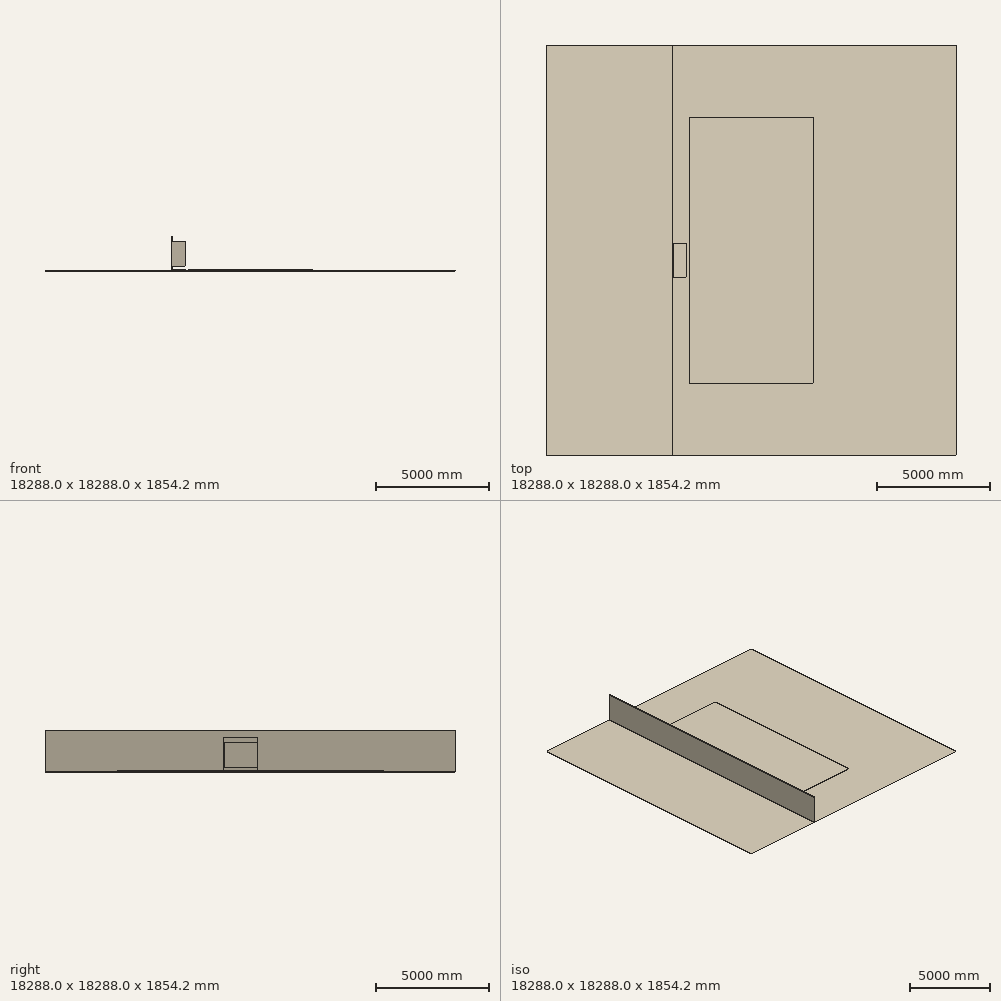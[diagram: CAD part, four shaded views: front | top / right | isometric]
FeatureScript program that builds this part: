
annotation { "Feature Type Name" : "Feature", "Feature Type Description" : "" }
export const myFeature = defineFeature(function(context is Context, id is Id, definition is map)
    precondition{}
    {
        {
            var Q0;
            Q0=qCreatedBy(makeId("Top.planeOp"),FACE);
            var sketch = newSketch(context, id + "F0", { "sketchPlane" : qUnion([Q0])});
            skLineSegment(sketch, "E0.bottom", {"start": v(-9144, 9144) * mm, "end": v(9144, 9144) * mm});
            skLineSegment(sketch, "E0.top", {"start": v(-9144, -9144) * mm, "end": v(9144, -9144) * mm});
            skLineSegment(sketch, "E0.left", {"start": v(-9144, 9144) * mm, "end": v(-9144, -9144) * mm});
            skLineSegment(sketch, "E0.right", {"start": v(9144, 9144) * mm, "end": v(9144, -9144) * mm});
            skSolve(sketch);
        }
        {
            var Q0;
            Q0=makeQuery(id+"F0.imprint","IMPRINT",FACE,{"disambiguationData":[TD([[makeQuery(id+"F0.imprint","IMPRINT",EDGE,{"derivedFrom":sQuery(id+"F0.wireOp",EDGE,"E0.bottom")}),-1.0]])]});
            extrude(context, id + "F1", {"entities" : qUnion([Q0]), "depth" : 25.4 * mm});
        }
        {
            var Q0;
            Q0=makeQuery(id+"F1.opExtrude","CAP_FACE",FACE,{"disambiguationData":[OSD([sQuery(id+"F0.wireOp",EDGE,"E0.bottom"),sQuery(id+"F0.wireOp",EDGE,"E0.top"),sQuery(id+"F0.wireOp",EDGE,"E0.left"),sQuery(id+"F0.wireOp",EDGE,"E0.right")])],"isStart":false});
            var sketch = newSketch(context, id + "F2", { "sketchPlane" : qUnion([Q0])});
            skLineSegment(sketch, "E1.bottom", {"start": v(-2743.2, 5943.6) * mm, "end": v(2743.2, 5943.6) * mm});
            skLineSegment(sketch, "E1.top", {"start": v(-2743.2, -5943.6) * mm, "end": v(2743.2, -5943.6) * mm});
            skLineSegment(sketch, "E1.left", {"start": v(-2743.2, 5943.6) * mm, "end": v(-2743.2, -5943.6) * mm});
            skLineSegment(sketch, "E1.right", {"start": v(2743.2, 5943.6) * mm, "end": v(2743.2, -5943.6) * mm});
            skSolve(sketch);
        }
        {
            var Q0;
            Q0=makeQuery(id+"F2.imprint","IMPRINT",FACE,{"disambiguationData":[TD([[makeQuery(id+"F2.imprint","IMPRINT",EDGE,{"derivedFrom":sQuery(id+"F2.wireOp",EDGE,"E1.bottom")}),-1.0]])]});
            extrude(context, id + "F3", {"entities" : qUnion([Q0]), "operationType" : NewBodyOperationType.ADD, "depth" : 50.8 * mm});
        }
        {
            var Q0;
            Q0=makeQuery(id+"F1.opExtrude","CAP_FACE",FACE,{"disambiguationData":[OSD([sQuery(id+"F0.wireOp",EDGE,"E0.bottom"),sQuery(id+"F0.wireOp",EDGE,"E0.top"),sQuery(id+"F0.wireOp",EDGE,"E0.left"),sQuery(id+"F0.wireOp",EDGE,"E0.right")])],"isStart":false});
            var sketch = newSketch(context, id + "F4", { "sketchPlane" : qUnion([Q0])});
            skLineSegment(sketch, "E2.bottom", {"start": v(-3505.2, 330.2) * mm, "end": v(-2895.6, 330.2) * mm});
            skLineSegment(sketch, "E2.top", {"start": v(-3505.2, -1193.8) * mm, "end": v(-2895.6, -1193.8) * mm});
            skLineSegment(sketch, "E2.left", {"start": v(-3505.2, 330.2) * mm, "end": v(-3505.2, -1193.8) * mm});
            skLineSegment(sketch, "E2.right", {"start": v(-2895.6, 330.2) * mm, "end": v(-2895.6, -1193.8) * mm});
            skSolve(sketch);
        }
        {
            var Q0;
            Q0=makeQuery(id+"F4.imprint","IMPRINT",FACE,{"disambiguationData":[TD([[makeQuery(id+"F4.imprint","IMPRINT",EDGE,{"derivedFrom":sQuery(id+"F4.wireOp",EDGE,"E2.bottom")}),-1.0]])]});
            extrude(context, id + "F5", {"entities" : qUnion([Q0]), "operationType" : NewBodyOperationType.ADD, "depth" : 1524 * mm});
        }
        {
            var Q0;
            Q0=makeQuery(id+"F5.opExtrude","SWEPT_FACE",FACE,{"disambiguationData":[OSD([sQuery(id+"F4.wireOp",EDGE,"E2.right")])]});
            var sketch = newSketch(context, id + "F6", { "sketchPlane" : qUnion([Q0])});
            skLineSegment(sketch, "E3.bottom", {"start": v(-1366.04, 1549.4) * mm, "end": v(481.07, 1549.4) * mm});
            skLineSegment(sketch, "E3.top", {"start": v(-1366.04, 1346.2) * mm, "end": v(481.07, 1346.2) * mm});
            skLineSegment(sketch, "E3.left", {"start": v(-1366.04, 1549.4) * mm, "end": v(-1366.04, 1346.2) * mm});
            skLineSegment(sketch, "E3.right", {"start": v(481.07, 1549.4) * mm, "end": v(481.07, 1346.2) * mm});
            skLineSegment(sketch, "E4.bottom", {"start": v(-1193.8, 209.09) * mm, "end": v(330.2, 209.09) * mm});
            skLineSegment(sketch, "E4.top", {"start": v(-1193.8, 82.09) * mm, "end": v(330.2, 82.09) * mm});
            skLineSegment(sketch, "E4.left", {"start": v(-1193.8, 209.09) * mm, "end": v(-1193.8, 82.09) * mm});
            skLineSegment(sketch, "E4.right", {"start": v(330.2, 209.09) * mm, "end": v(330.2, 82.09) * mm});
            skSolve(sketch);
        }
        {
            var Q0;
            {var subQ3=sQuery(id+"F6.wireOp",EDGE,"E3.left");Q0=makeQuery(id+"F6.imprint","IMPRINT",FACE,{"disambiguationData":[TD([[makeQuery(id+"F6.imprint","IMPRINT",EDGE,{"derivedFrom":subQ3}),1.0]])]});}
            var Q1;
            {var subQ0=sQuery(id+"F6.wireOp",EDGE,"E3.bottom");var subQ1=sQuery(id+"F4.wireOp",EDGE,"E2.right");var subQ2=makeQuery(id+"F5.opExtrude","SWEPT_EDGE",EDGE,{"disambiguationData":[OSD([sQuery(id+"F4.wireOp",EDGE,"E2.bottom"),subQ1])]});var subQ3=makeQuery(id+"F6.imprint","INTERSECT",VERTEX,{"derivedFrom":[subQ2,subQ0]});var subQ4=makeQuery(id+"F5.opExtrude","SWEPT_EDGE",EDGE,{"disambiguationData":[OSD([sQuery(id+"F4.wireOp",EDGE,"E2.top"),subQ1])]});var subQ5=makeQuery(id+"F6.imprint","INTERSECT",VERTEX,{"derivedFrom":[subQ4,subQ0]});Q1=makeQuery(id+"F6.imprint","IMPRINT",FACE,{"disambiguationData":[TD([[makeQuery(id+"F6.imprint","IMPRINT",EDGE,{"disambiguationData":[TD([[subQ3,-1.0],[subQ5,1.0]])],"derivedFrom":subQ0}),1.0]])]});}
            var Q2;
            Q2=makeQuery(id+"F6.imprint","IMPRINT",FACE,{"disambiguationData":[TD([[makeQuery(id+"F6.imprint","IMPRINT",EDGE,{"derivedFrom":sQuery(id+"F6.wireOp",EDGE,"E4.bottom")}),-1.0]])]});
            extrude(context, id + "F7", {"entities" : qUnion([Q0, Q1, Q2]), "operationType" : NewBodyOperationType.REMOVE, "oppositeDirection" : true, "depth" : 584.2 * mm});
        }
        {
            var Q0;
            Q0=makeQuery(id+"F7.boolean.opBoolean","SPLIT",FACE,{"disambiguationData":[TD([makeQuery(id+"F7.opExtrude","SWEPT_FACE",FACE,{"disambiguationData":[OSD([sQuery(id+"F6.wireOp",EDGE,"E3.top")])]})])],"derivedFrom":makeQuery(id+"F5.opExtrude","SWEPT_FACE",FACE,{"disambiguationData":[OSD([sQuery(id+"F4.wireOp",EDGE,"E2.right")])]})});
            var sketch = newSketch(context, id + "F8", { "sketchPlane" : qUnion([Q0])});
            skLineSegment(sketch, "E5.bottom", {"start": v(-1168.4, 1320.8) * mm, "end": v(304.8, 1320.8) * mm});
            skLineSegment(sketch, "E5.top", {"start": v(-1168.4, 234.49) * mm, "end": v(304.8, 234.49) * mm});
            skLineSegment(sketch, "E5.left", {"start": v(-1168.4, 1320.8) * mm, "end": v(-1168.4, 234.49) * mm});
            skLineSegment(sketch, "E5.right", {"start": v(304.8, 1320.8) * mm, "end": v(304.8, 234.49) * mm});
            skSolve(sketch);
        }
        {
            var Q0;
            Q0=makeQuery(id+"F8.imprint","IMPRINT",FACE,{"disambiguationData":[TD([[makeQuery(id+"F8.imprint","IMPRINT",EDGE,{"derivedFrom":sQuery(id+"F8.wireOp",EDGE,"E5.bottom")}),-1.0]])]});
            extrude(context, id + "F9", {"entities" : qUnion([Q0]), "operationType" : NewBodyOperationType.REMOVE, "oppositeDirection" : true, "depth" : 508 * mm});
        }
        {
            var Q0;
            Q0=makeQuery(id+"F1.opExtrude","CAP_FACE",FACE,{"disambiguationData":[OSD([sQuery(id+"F0.wireOp",EDGE,"E0.bottom"),sQuery(id+"F0.wireOp",EDGE,"E0.top"),sQuery(id+"F0.wireOp",EDGE,"E0.left"),sQuery(id+"F0.wireOp",EDGE,"E0.right")])],"isStart":false});
            var sketch = newSketch(context, id + "F10", { "sketchPlane" : qUnion([Q0])});
            skLineSegment(sketch, "E6", {"start": v(-3505.2, 9144) * mm, "end": v(-3505.2, -9144) * mm});
            skLineSegment(sketch, "E7", {"start": v(-3543.3, 9144) * mm, "end": v(-3543.3, -9144) * mm});
            skLineSegment(sketch, "E8", {"start": v(-3543.3, 9144) * mm, "end": v(-3505.2, 9144) * mm});
            skLineSegment(sketch, "E9", {"start": v(-3543.3, -9144) * mm, "end": v(-3505.2, -9144) * mm});
            skSolve(sketch);
        }
        {
            var Q0;
            Q0=makeQuery(id+"F10.imprint","IMPRINT",FACE,{"disambiguationData":[TD([[makeQuery(id+"F10.imprint","IMPRINT",EDGE,{"derivedFrom":sQuery(id+"F10.wireOp",EDGE,"E7")}),1.0]])]});
            extrude(context, id + "F11", {"entities" : qUnion([Q0]), "operationType" : NewBodyOperationType.ADD, "depth" : 1828.8 * mm});
        }
    });
